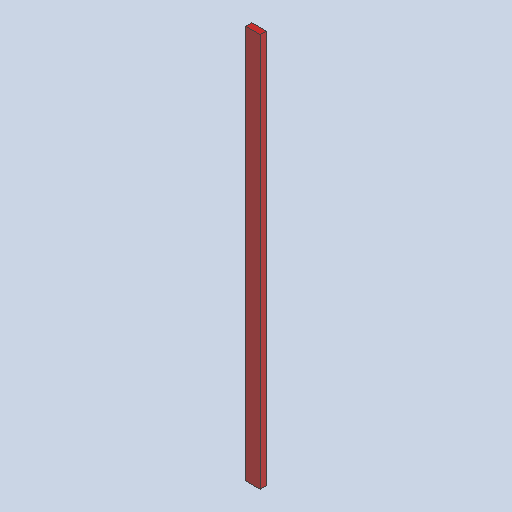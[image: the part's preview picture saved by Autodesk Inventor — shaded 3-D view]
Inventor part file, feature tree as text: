
AUTODESK INVENTOR PART (.ipt)
format: ipt  version: 2025 (Build 290162000, 162)  size: 84,480 bytes
history: native  units: in
note: dims shown in document units (in); Inventor stores cm internally (conversion verified against a paired STEP export)
features: other x4, sketch x1
ambient origin geometry x8: Origin, YZ Plane, XZ Plane, XY Plane, X Axis, Y Axis, Z Axis, Center Point
bodies: Solid1 (feature_tree)
feature tree (5):
  other  "8'x2x4.ipt"
  other  "Solid1::8'x2x4.ipt"
  other  "TaggingFeature1"
  sketch  "Sketch1"  dims[d0=0.3937in]
  other  "Finish1"
